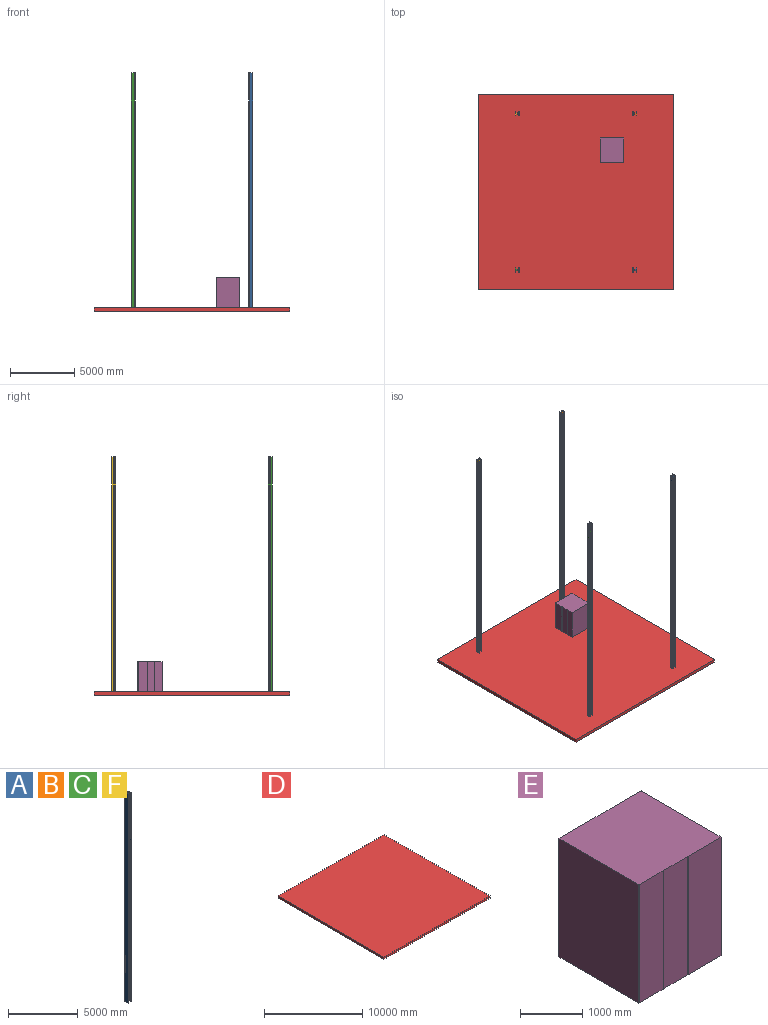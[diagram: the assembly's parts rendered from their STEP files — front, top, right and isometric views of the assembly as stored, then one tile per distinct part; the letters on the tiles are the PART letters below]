
ASSEMBLY  parts=6 mates=5
PART A: 18 faces, bbox 304.8x304.8x18288 mm
  f0: plane 18288x107.95mm, normal (1,0,0), area 1974189.6mm2, adj f11,f12,f13,f14
  f1: plane 18288x228.6mm, normal (0,-1,0), area 4180636.8mm2, adj f12,f13,f14,f17
  f2: plane 18288x107.95mm, normal (-1,0,0), area 1974189.6mm2, adj f3,f12,f13,f17
  f3: plane 18288x25.4mm, normal (0,-1,0), area 464515.2mm2, adj f2,f4,f12,f13
  f4: plane 18288x304.8mm, normal (1,0,0), area 5574182.4mm2, adj f3,f5,f12,f13
  f5: plane 18288x25.4mm, normal (0,1,0), area 464515.2mm2, adj f4,f6,f12,f13
  f6: plane 18288x107.95mm, normal (-1,0,0), area 1974189.6mm2, adj f5,f12,f13,f16
  f7: plane 18288x228.6mm, normal (0,1,0), area 4180636.8mm2, adj f12,f13,f15,f16
  f8: plane 18288x107.95mm, normal (1,0,0), area 1974189.6mm2, adj f9,f12,f13,f15
  f9: plane 18288x25.4mm, normal (0,1,0), area 464515.2mm2, adj f8,f10,f12,f13
  f10: plane 18288x304.8mm, normal (-1,0,0), area 5574182.4mm2, adj f9,f11,f12,f13
  f11: plane 18288x25.4mm, normal (0,-1,0), area 464515.2mm2, adj f0,f10,f12,f13
  f12: plane 304.8x304.8mm, normal (0,0,1), area 31751.3mm2, adj f0,f1,f2,f3,f4,f5,f6,f7
  f13: plane 304.8x304.8mm, normal (0,0,-1), area 31751.3mm2, adj f0,f1,f2,f3,f4,f5,f6,f7
  f14: cylinder r=12.7mm len=18288mm, axis (0,0,1), area 364829.4mm2, adj f0,f1,f12,f13
  f15: cylinder r=12.7mm len=18288mm, axis (0,0,-1), area 364829.4mm2, adj f7,f8,f12,f13
  f16: cylinder r=12.7mm len=18288mm, axis (0,0,1), area 364829.4mm2, adj f6,f7,f12,f13
  f17: cylinder r=12.7mm len=18288mm, axis (0,0,-1), area 364829.4mm2, adj f1,f2,f12,f13
PART B: same geometry as A
PART C: same geometry as A
PART D: 6 faces, bbox 15240x15240x254 mm
  f0: plane 15240x254mm, normal (0,-1,0), area 3870960mm2, adj f1,f3,f4,f5
  f1: plane 15240x254mm, normal (1,0,0), area 3870960mm2, adj f0,f2,f4,f5
  f2: plane 15240x254mm, normal (0,1,0), area 3870960mm2, adj f1,f3,f4,f5
  f3: plane 15240x254mm, normal (-1,0,0), area 3870960mm2, adj f0,f2,f4,f5
  f4: plane 15240x15240mm, normal (0,0,-1), area 232257600mm2, adj f0,f1,f2,f3
  f5: plane 15240x15240mm, normal (0,0,1), area 232257600mm2, adj f0,f1,f2,f3
PART E: 22 faces, bbox 1879.6x1828.8x2336.8 mm
  f0: cylinder r=6.35mm len=2336.8mm, axis (0,0,-1), area 23308.5mm2, adj f1,f19,f20,f21
  f1: cylinder r=6.35mm len=2336.8mm, axis (0,0,-1), area 23308.5mm2, adj f0,f2,f20,f21
  f2: plane 2336.8x546.1mm, normal (0,-1,0), area 1276126.5mm2, adj f1,f3,f20,f21
  f3: cylinder r=6.35mm len=2336.8mm, axis (0,0,-1), area 23308.5mm2, adj f2,f4,f20,f21
  f4: cylinder r=6.35mm len=2336.8mm, axis (0,0,-1), area 23308.5mm2, adj f3,f5,f20,f21
  f5: plane 2336.8x749.3mm, normal (0,-1,0), area 1750964.2mm2, adj f4,f6,f20,f21
  f6: cylinder r=6.35mm len=2336.8mm, axis (0,0,-1), area 23308.5mm2, adj f5,f7,f20,f21
  f7: plane 2336.8x1816.1mm, normal (1,0,0), area 4243862.5mm2, adj f6,f8,f20,f21
  f8: cylinder r=6.35mm len=2336.8mm, axis (0,0,-1), area 23308.5mm2, adj f7,f9,f20,f21
  f9: plane 2336.8x749.3mm, normal (0,1,0), area 1750964.2mm2, adj f8,f10,f20,f21
  f10: cylinder r=6.35mm len=2336.8mm, axis (0,0,-1), area 23308.5mm2, adj f9,f11,f20,f21
  f11: cylinder r=6.35mm len=2336.8mm, axis (0,0,-1), area 23308.5mm2, adj f10,f12,f20,f21
  f12: plane 2336.8x546.1mm, normal (0,1,0), area 1276126.5mm2, adj f11,f13,f20,f21
  f13: cylinder r=6.35mm len=2336.8mm, axis (0,0,-1), area 23308.5mm2, adj f12,f14,f20,f21
  f14: cylinder r=6.35mm len=2336.8mm, axis (0,0,-1), area 23308.5mm2, adj f13,f15,f20,f21
  f15: plane 2336.8x546.1mm, normal (0,1,0), area 1276126.5mm2, adj f14,f16,f20,f21
  f16: cylinder r=6.35mm len=2336.8mm, axis (0,0,-1), area 23308.5mm2, adj f15,f17,f20,f21
  f17: plane 2336.8x1816.1mm, normal (-1,0,0), area 4243862.5mm2, adj f16,f18,f20,f21
  f18: cylinder r=6.35mm len=2336.8mm, axis (0,0,-1), area 23308.5mm2, adj f17,f19,f20,f21
  f19: plane 2336.8x546.1mm, normal (0,-1,0), area 1276126.5mm2, adj f0,f18,f20,f21
  f20: plane 1879.6x1828.8mm, normal (0,0,1), area 3437308.6mm2, adj f0,f1,f2,f3,f4,f5,f6,f7
  f21: plane 1879.6x1828.8mm, normal (0,0,-1), area 3437308.6mm2, adj f0,f1,f2,f3,f4,f5,f6,f7
PART F: same geometry as A
PLACE A t=(4572,-6096,0)mm
PLACE B t=(4572,6096,0)mm
PLACE C t=(-4572,-6096,0)mm
PLACE D at identity
PLACE E rot(axis=(0,0,1),90deg) t=(2818.01,3166.71,0)mm
PLACE F t=(-4572,6096,0)mm
MATE fastened D.f5 <-> C.f13  axis (0,0,1) through (-4572,-6096,0)mm
MATE fastened D.f5 <-> F.f13  axis (0,0,1) through (-4572,6096,0)mm
MATE fastened D.f5 <-> B.f13  axis (0,0,1) through (4572,6096,0)mm
MATE fastened D.f5 <-> A.f13  axis (0,0,1) through (4572,-6096,0)mm
MATE planar D.f5 <-> E.f21  axis (0,0,1) through (0,0,0)mm
